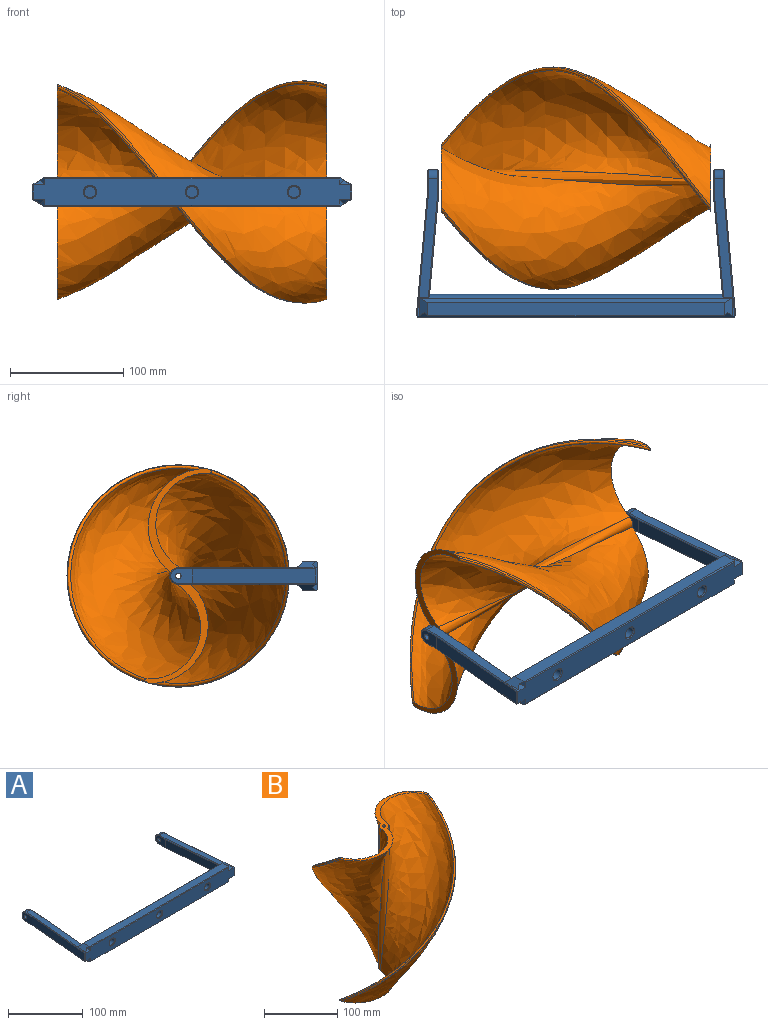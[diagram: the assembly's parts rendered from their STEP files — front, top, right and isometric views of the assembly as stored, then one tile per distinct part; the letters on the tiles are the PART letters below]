
ASSEMBLY  parts=2 mates=1
PART A: 81 faces, bbox 281.8x130x25 mm
  f0: plane 16.5x1.5mm, normal (0,0,-1), area 12.4mm2, adj f47,f52,f80
  f1: plane 16.5x1.5mm, normal (0,0,1), area 12.4mm2, adj f59,f64,f79
  f2: plane 258.36x0.89mm, normal (0,1,0), area 229.2mm2, adj f6,f16,f75,f76
  f3: plane 280x23.17mm, normal (0,-1,0), area 5960.8mm2, adj f48,f51,f52,f53,f54,f55,f56,f57
  f4: plane 262.09x11.59mm, normal (0,0,1), area 3036.7mm2, adj f13,f55,f57,f78,f79
  f5: plane 262.09x11.59mm, normal (0,0,-1), area 3036.7mm2, adj f12,f54,f56,f77,f80
  f6: plane 91.88x13.17mm, normal (1,-0.09,0), area 1197.9mm2, adj f2,f11,f30,f33,f75,f76
  f7: plane 121.59x18.09mm, normal (0,0,1), area 871.8mm2, adj f14,f33,f34,f41,f44,f46,f51,f76
  f8: plane 105.06x16.58mm, normal (0,0,-1), area 858mm2, adj f14,f30,f31,f42,f45,f47,f75
  f9: plane 19.05x13.17mm, normal (-1,0,0), area 210.2mm2, adj f15,f40,f41,f42,f43
  f10: plane 108.96x13.17mm, normal (-1,0.09,0), area 1441.3mm2, adj f43,f46,f47,f48
  f11: plane 19.09x13.17mm, normal (1,0,0), area 210.8mm2, adj f6,f15,f31,f32,f34
  f12: plane 274.77x4.28mm, normal (0,0.71,-0.71), area 1624.1mm2, adj f5,f75,f77,f80
  f13: plane 274.77x4.28mm, normal (0,0.71,0.71), area 1624.1mm2, adj f4,f76,f78,f79
  f14: cylinder r=7.5mm len=15mm, axis (1,0,0), area 192.6mm2, adj f7,f8,f32,f40
  f15: cylinder r=2.65mm len=10mm, axis (1,0,0), area 166.5mm2, adj f9,f11
  f16: plane 91.88x13.17mm, normal (-1,-0.09,0), area 1197.9mm2, adj f2,f21,f35,f38,f75,f76
  f17: plane 105.06x16.58mm, normal (0,0,1), area 858mm2, adj f22,f35,f36,f64,f67,f69,f76
  f18: plane 121.59x18.09mm, normal (0,0,-1), area 871.8mm2, adj f22,f38,f39,f60,f65,f68,f70,f75
  f19: plane 19.05x13.17mm, normal (1,0,0), area 210.2mm2, adj f23,f66,f69,f70,f71
  f20: plane 108.96x13.17mm, normal (1,0.09,0), area 1441.3mm2, adj f61,f64,f65,f66
  f21: plane 19.09x13.17mm, normal (-1,0,0), area 210.8mm2, adj f16,f23,f36,f37,f39
  f22: cylinder r=7.5mm len=15mm, axis (-1,0,0), area 192.6mm2, adj f17,f18,f37,f71
  f23: cylinder r=2.65mm len=10mm, axis (-1,0,0), area 166.5mm2, adj f19,f21
  f24: cylinder r=5mm len=10mm, axis (0,-1,0), area 285.5mm2, adj f25,f72
  f25: plane 10x10mm, normal (0,-1,0), area 78.5mm2, adj f24
  f26: cylinder r=5mm len=10mm, axis (0,-1,0), area 285.5mm2, adj f27,f73
  f27: plane 10x10mm, normal (0,-1,0), area 78.5mm2, adj f26
  f28: cylinder r=5mm len=10mm, axis (0,-1,0), area 285.5mm2, adj f29,f74
  f29: plane 10x10mm, normal (0,-1,0), area 78.5mm2, adj f28
  f30: plane 92.6x9.33mm, normal (0.7,-0.06,-0.71), area 119.6mm2, adj f6,f8,f31,f75
  f31: plane 12.5x0.91mm, normal (0.71,0,-0.71), area 16.1mm2, adj f8,f11,f30,f32
  f32: cone r=6.59mm half-angle=45deg, axis (-1,0,0), area 28.6mm2, adj f11,f14,f31,f34
  f33: plane 92.6x9.33mm, normal (0.7,-0.06,0.71), area 119.6mm2, adj f6,f7,f34,f76
  f34: plane 12.5x0.91mm, normal (0.71,0,0.71), area 16.1mm2, adj f7,f11,f32,f33
  f35: plane 92.6x9.33mm, normal (-0.7,-0.06,0.71), area 119.6mm2, adj f16,f17,f36,f76
  f36: plane 12.5x0.91mm, normal (-0.71,0,0.71), area 16.1mm2, adj f17,f21,f35,f37
  f37: cone r=7.5mm half-angle=45deg, axis (1,0,0), area 28.6mm2, adj f21,f22,f36,f39
  f38: plane 92.6x9.33mm, normal (-0.7,-0.06,-0.71), area 119.6mm2, adj f16,f18,f39,f75
  f39: plane 12.5x0.91mm, normal (-0.71,0,-0.71), area 16.1mm2, adj f18,f21,f37,f38
  f40: cone r=6.59mm half-angle=45deg, axis (1,0,0), area 28.6mm2, adj f9,f14,f41,f42
  f41: plane 12.46x0.91mm, normal (-0.71,0,0.71), area 16.1mm2, adj f7,f9,f40,f44
  f42: plane 12.46x0.91mm, normal (-0.71,0,-0.71), area 16.1mm2, adj f8,f9,f40,f45
  f43: plane 13.17x0.08mm, normal (-1,0.05,0), area 1.1mm2, adj f9,f10,f44,f45
  f44: plane 0.92x0.91mm, normal (-0.71,0.03,0.71), area 0.2mm2, adj f7,f41,f43,f46
  f45: plane 0.92x0.91mm, normal (-0.71,0.03,-0.71), area 0.2mm2, adj f8,f42,f43,f47
  f46: plane 109.05x10.82mm, normal (-0.7,0.06,0.71), area 141.3mm2, adj f7,f10,f44,f49
  f47: plane 109.05x10.82mm, normal (-0.7,0.06,-0.71), area 141.3mm2, adj f0,f8,f10,f45,f50,f75,f80
  f48: plane 13.17x1mm, normal (-0.74,-0.67,0), area 17.8mm2, adj f3,f10,f49,f50
  f49: plane 1x0.91mm, normal (-0.61,-0.56,0.56), area 0.7mm2, adj f46,f48,f51
  f50: plane 1x0.91mm, normal (-0.61,-0.56,-0.56), area 0.7mm2, adj f47,f48,f52
  f51: plane 9.91x3.9mm, normal (0,-0.71,0.71), area 27.9mm2, adj f3,f7,f49,f53,f78
  f52: plane 9.91x3.93mm, normal (0,-0.71,-0.71), area 28.2mm2, adj f0,f3,f50,f54,f80
  f53: plane 5.91x3.9mm, normal (-0.71,-0.71,0), area 17mm2, adj f3,f51,f55,f78
  f54: plane 5.91x3.93mm, normal (-0.71,-0.71,0), area 17.3mm2, adj f3,f5,f52,f56,f80
  f55: plane 262x0.91mm, normal (0,-0.71,0.71), area 337.2mm2, adj f3,f4,f53,f57
  f56: plane 262x0.91mm, normal (0,-0.71,-0.71), area 337.2mm2, adj f3,f5,f54,f58
  f57: plane 5.91x3.93mm, normal (0.71,-0.71,0), area 17.3mm2, adj f3,f4,f55,f59,f79
  f58: plane 5.91x3.9mm, normal (0.71,-0.71,0), area 17mm2, adj f3,f56,f60,f77
  f59: plane 9.91x3.93mm, normal (0,-0.71,0.71), area 28.2mm2, adj f1,f3,f57,f62,f79
  f60: plane 9.91x3.9mm, normal (0,-0.71,-0.71), area 27.9mm2, adj f3,f18,f58,f63,f77
  f61: plane 13.17x1mm, normal (0.74,-0.67,0), area 17.8mm2, adj f3,f20,f62,f63
  f62: plane 1x0.91mm, normal (0.61,-0.56,0.56), area 0.7mm2, adj f59,f61,f64
  f63: plane 1x0.91mm, normal (0.61,-0.56,-0.56), area 0.7mm2, adj f60,f61,f65
  f64: plane 109.05x10.82mm, normal (0.7,0.06,0.71), area 141.3mm2, adj f1,f17,f20,f62,f67,f76,f79
  f65: plane 109.05x10.82mm, normal (0.7,0.06,-0.71), area 141.3mm2, adj f18,f20,f63,f68
  f66: plane 13.17x0.08mm, normal (1,0.05,0), area 1.1mm2, adj f19,f20,f67,f68
  f67: plane 0.92x0.91mm, normal (0.71,0.03,0.71), area 0.2mm2, adj f17,f64,f66,f69
  f68: plane 0.92x0.91mm, normal (0.71,0.03,-0.71), area 0.2mm2, adj f18,f65,f66,f70
  f69: plane 12.46x0.91mm, normal (0.71,0,0.71), area 16.1mm2, adj f17,f19,f67,f71
  f70: plane 12.46x0.91mm, normal (0.71,0,-0.71), area 16.1mm2, adj f18,f19,f68,f71
  f71: cone r=7.5mm half-angle=45deg, axis (-1,0,0), area 28.6mm2, adj f19,f22,f69,f70
  f72: cone r=5mm half-angle=45deg, axis (0,-1,0), area 44.3mm2, adj f3,f24
  f73: cone r=5mm half-angle=45deg, axis (0,-1,0), area 44.3mm2, adj f3,f26
  f74: cone r=5mm half-angle=45deg, axis (0,-1,0), area 44.3mm2, adj f3,f28
  f75: cylinder r=11mm len=276.91mm, axis (-1,0,0), area 2251.5mm2, adj f2,f6,f8,f12,f16,f18,f30,f38
  f76: cylinder r=11mm len=276.91mm, axis (-1,0,0), area 2251.5mm2, adj f2,f6,f7,f13,f16,f17,f33,f35
  f77: plane 16.53x7.41mm, normal (0.56,0,-0.83), area 112.6mm2, adj f5,f12,f18,f58,f60,f75
  f78: plane 16.53x7.41mm, normal (-0.56,0,0.83), area 112.6mm2, adj f4,f7,f13,f51,f53,f76
  f79: plane 16.52x7.41mm, normal (0.56,0,0.83), area 112.3mm2, adj f1,f4,f13,f57,f59,f64,f76
  f80: plane 16.52x7.41mm, normal (-0.56,0,-0.83), area 112.3mm2, adj f0,f5,f12,f47,f52,f54,f75
PART B: 13 faces, bbox 243.4x244.1x269 mm
  f0: cylinder r=7mm len=238mm, axis (0,0,-1), area 2616.9mm2, adj f2,f3,f4,f7
  f1: cylinder r=7mm len=238mm, axis (0,0,-1), area 2616.9mm2, adj f2,f3,f6,f8
  f2: plane 206.19x104.35mm, normal (0,0,1), area 1619.3mm2, adj f0,f1,f4,f5,f6,f7,f8,f9
  f3: plane 206.19x104.35mm, normal (0,0,-1), area 1619.4mm2, adj f0,f1,f4,f5,f6,f7,f8,f9
  f4: bspline ~256.31x212.59mm, area 32319.2mm2, adj f0,f2,f3,f11
  f5: bspline ~256.31x195.82mm, area 690.9mm2, adj f2,f3,f6,f11
  f6: bspline ~238x198.67mm, area 34271.9mm2, adj f1,f2,f3,f5
  f7: bspline ~238x198.67mm, area 34271.9mm2, adj f0,f2,f3,f9
  f8: bspline ~256.31x212.59mm, area 32319.2mm2, adj f1,f2,f3,f12
  f9: bspline ~256.31x195.82mm, area 690.9mm2, adj f2,f3,f7,f12
  f10: cylinder r=2.55mm len=238mm, axis (0,0,-1), area 3813.3mm2, adj f2,f3
  f11: bspline ~246.21x194.85mm, area 1474.8mm2, adj f2,f3,f4,f5
  f12: bspline ~246.21x194.85mm, area 1474.8mm2, adj f2,f3,f8,f9
PLACE A at identity fixed
PLACE B rot(axis=(0.2,-0.96,-0.2),92.4deg) t=(119,122.5,7.5)mm
MATE revolute A.f14 <-> B.f10  axis (1,0,0) through (-121,122.5,7.5)mm
